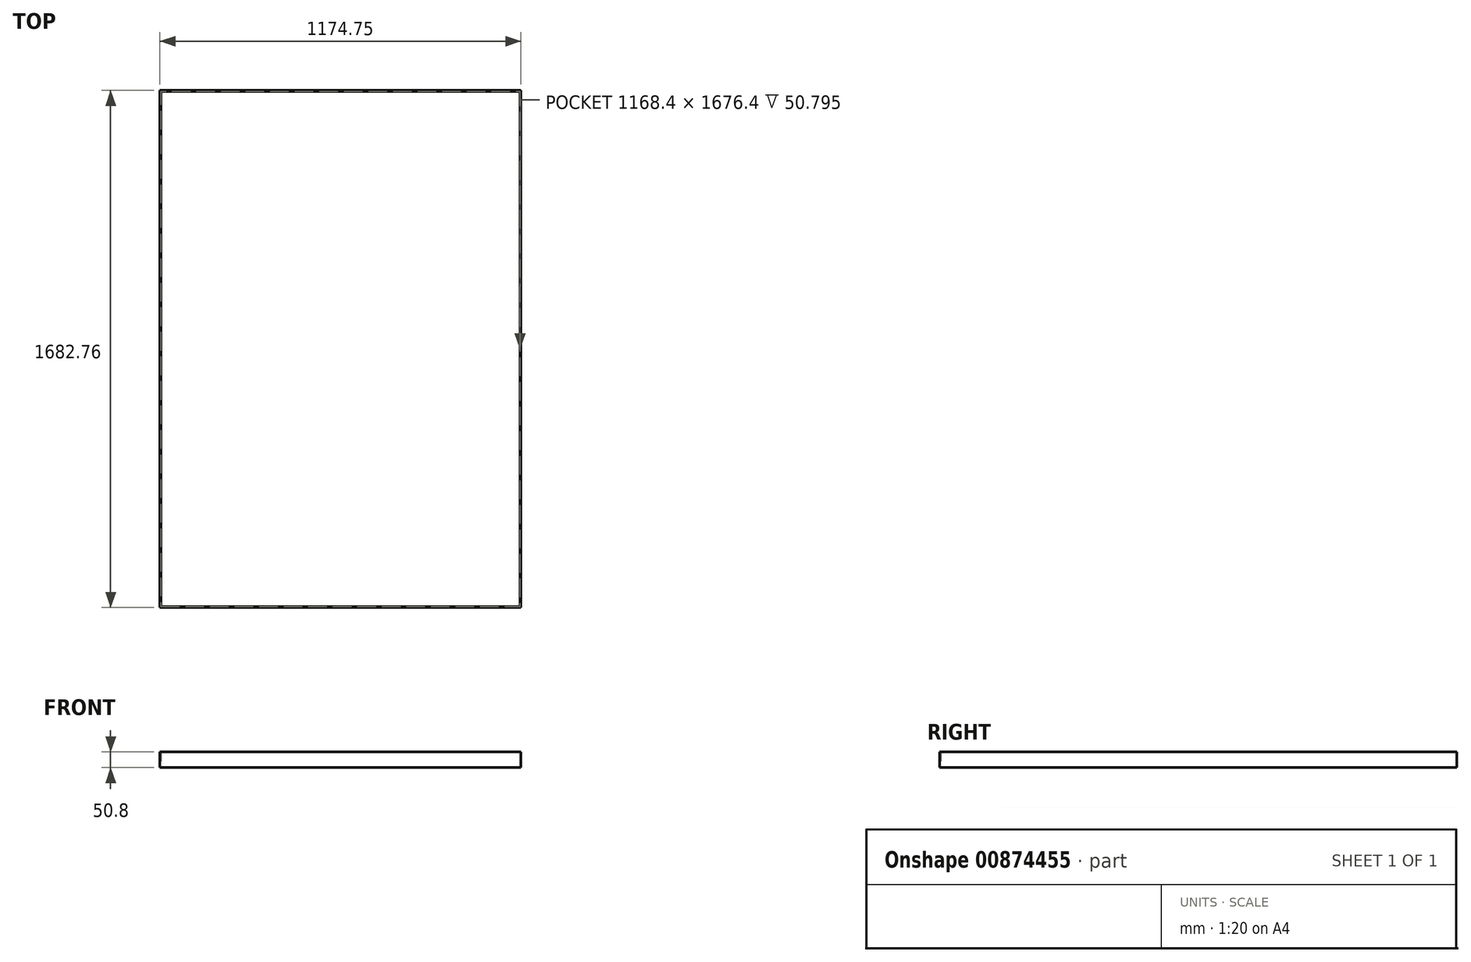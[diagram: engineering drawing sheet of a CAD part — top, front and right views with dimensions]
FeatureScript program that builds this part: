
annotation { "Feature Type Name" : "Feature", "Feature Type Description" : "" }
export const myFeature = defineFeature(function(context is Context, id is Id, definition is map)
    precondition{}
    {
        {
            var Q0;
            Q0=qCreatedBy(makeId("Top.planeOp"),FACE);
            var sketch = newSketch(context, id + "F0", { "sketchPlane" : qUnion([Q0])});
            skLineSegment(sketch, "E0.bottom", {"start": v(0, 0) * mm, "end": v(-1168.4, 0) * mm});
            skLineSegment(sketch, "E0.top", {"start": v(0, 1676.4) * mm, "end": v(-1168.4, 1676.4) * mm});
            skLineSegment(sketch, "E0.left", {"start": v(0, 0) * mm, "end": v(0, 1676.4) * mm});
            skLineSegment(sketch, "E0.right", {"start": v(-1168.4, 0) * mm, "end": v(-1168.4, 1676.4) * mm});
            skSolve(sketch);
        }
        {
            var Q0;
            Q0 = qSketchRegion(id + "F0", true);
            extrude(context, id + "F1", {"entities" : qUnion([Q0]), "depth" : 1 / 203.2 * mm, "offsetDistance" : 25.4 * mm});
        }
        {
            var Q0;
            Q0=qCreatedBy(makeId("Top.planeOp"),FACE);
            var sketch = newSketch(context, id + "F2", { "sketchPlane" : qUnion([Q0])});
            skLineSegment(sketch, "E1.bottom", {"start": v(0, 0) * mm, "end": v(-1168.4, 0) * mm});
            skLineSegment(sketch, "E1.top", {"start": v(0, -3.18) * mm, "end": v(-1168.4, -3.18) * mm});
            skLineSegment(sketch, "E1.left", {"start": v(0, 0) * mm, "end": v(0, -3.17) * mm});
            skLineSegment(sketch, "E1.right", {"start": v(-1168.4, 0) * mm, "end": v(-1168.4, -3.18) * mm});
            skLineSegment(sketch, "E2.bottom", {"start": v(-1168.4, -3.18) * mm, "end": v(-1171.58, -3.18) * mm});
            skLineSegment(sketch, "E2.top", {"start": v(-1168.4, 1679.58) * mm, "end": v(-1171.58, 1679.58) * mm});
            skLineSegment(sketch, "E2.left", {"start": v(-1168.4, -3.18) * mm, "end": v(-1168.4, 1679.58) * mm});
            skLineSegment(sketch, "E2.right", {"start": v(-1171.58, -3.17) * mm, "end": v(-1171.58, 1679.58) * mm});
            skLineSegment(sketch, "E3.bottom", {"start": v(-1168.4, 1679.58) * mm, "end": v(0, 1679.58) * mm});
            skLineSegment(sketch, "E3.top", {"start": v(-1168.4, 1676.4) * mm, "end": v(0, 1676.4) * mm});
            skLineSegment(sketch, "E3.left", {"start": v(-1168.4, 1679.58) * mm, "end": v(-1168.4, 1676.4) * mm});
            skLineSegment(sketch, "E3.right", {"start": v(0, 1679.58) * mm, "end": v(0, 1676.4) * mm});
            skLineSegment(sketch, "E4.bottom", {"start": v(0, 1679.58) * mm, "end": v(3.17, 1679.58) * mm});
            skLineSegment(sketch, "E4.top", {"start": v(0, -3.17) * mm, "end": v(3.18, -3.17) * mm});
            skLineSegment(sketch, "E4.left", {"start": v(0, 1679.58) * mm, "end": v(0, -3.17) * mm});
            skLineSegment(sketch, "E4.right", {"start": v(3.17, 1679.58) * mm, "end": v(3.18, -3.17) * mm});
            skSolve(sketch);
        }
        {
            var Q0;
            {var subQ3=sQuery(id+"F2.wireOp",EDGE,"E2.bottom");Q0=makeQuery(id+"F2.imprint","IMPRINT",FACE,{"disambiguationData":[TD([[makeQuery(id+"F2.imprint","IMPRINT",EDGE,{"derivedFrom":subQ3}),-1.0]])]});}
            var Q1;
            {var subQ0=sQuery(id+"F2.wireOp",EDGE,"E3.bottom");Q1=makeQuery(id+"F2.imprint","IMPRINT",FACE,{"disambiguationData":[TD([[makeQuery(id+"F2.imprint","IMPRINT",EDGE,{"derivedFrom":subQ0}),-1.0]])]});}
            var Q2;
            {var subQ3=sQuery(id+"F2.wireOp",EDGE,"E4.bottom");Q2=makeQuery(id+"F2.imprint","IMPRINT",FACE,{"disambiguationData":[TD([[makeQuery(id+"F2.imprint","IMPRINT",EDGE,{"derivedFrom":subQ3}),-1.0]])]});}
            var Q3;
            {var subQ0=sQuery(id+"F2.wireOp",EDGE,"E1.bottom");Q3=makeQuery(id+"F2.imprint","IMPRINT",FACE,{"disambiguationData":[TD([[makeQuery(id+"F2.imprint","IMPRINT",EDGE,{"derivedFrom":subQ0}),1.0]])]});}
            extrude(context, id + "F3", {"entities" : qUnion([Q0, Q1, Q2, Q3]), "operationType" : NewBodyOperationType.ADD, "depth" : 50.8 * mm, "offsetDistance" : 25.4 * mm});
        }
    });
